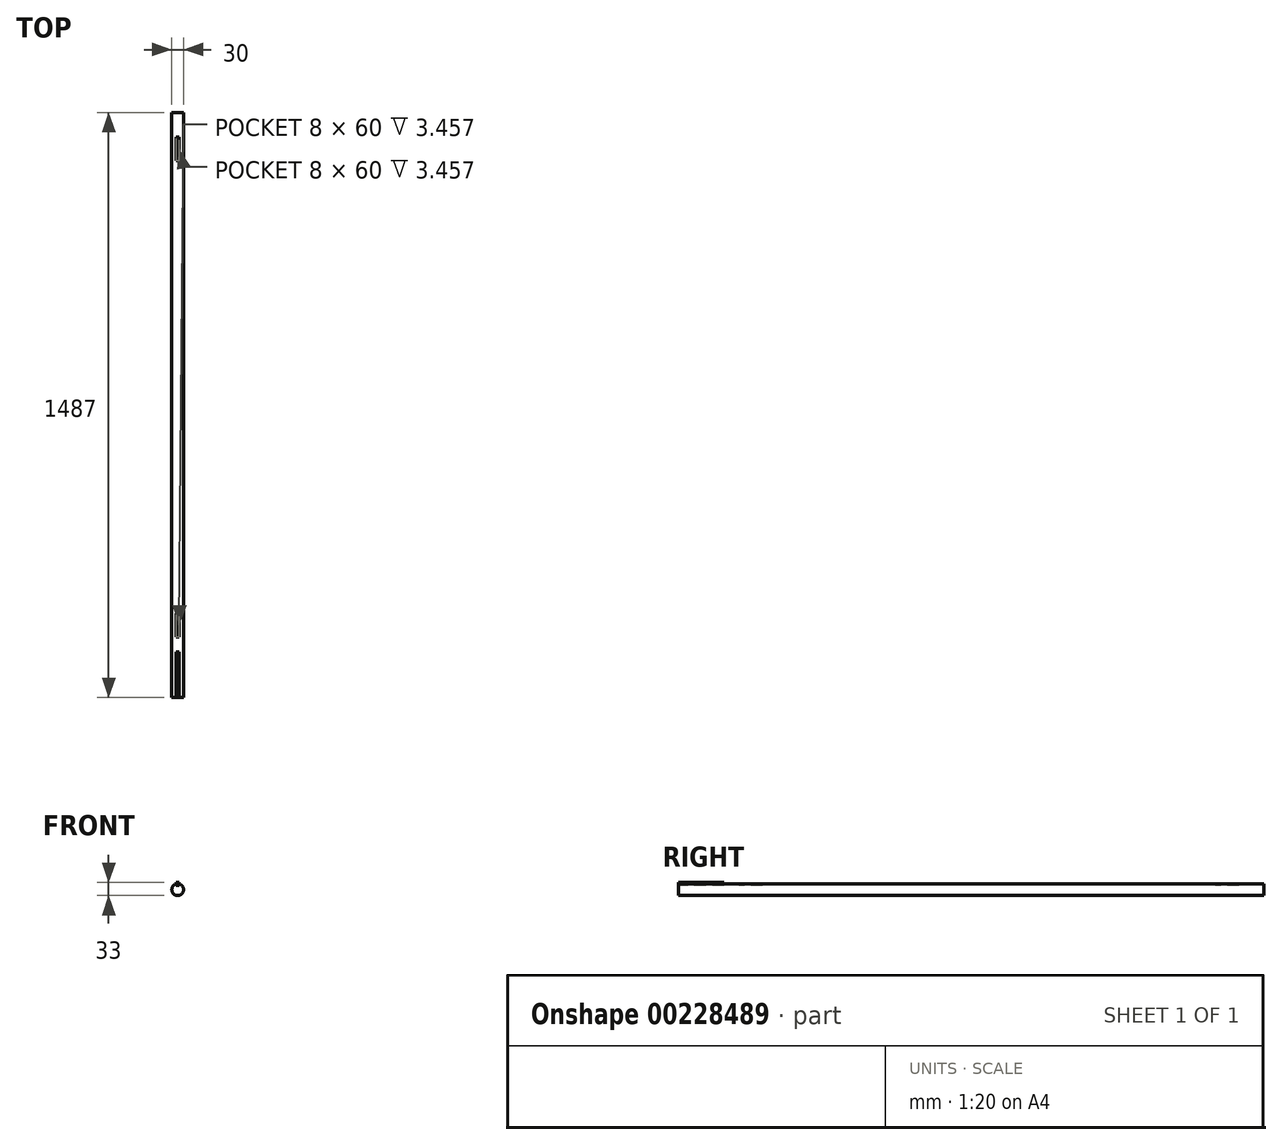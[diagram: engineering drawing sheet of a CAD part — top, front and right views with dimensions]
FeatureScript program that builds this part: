
annotation { "Feature Type Name" : "Feature", "Feature Type Description" : "" }
export const myFeature = defineFeature(function(context is Context, id is Id, definition is map)
    precondition{}
    {
        {
            var Q0;
            Q0=qCreatedBy(makeId("Front.planeOp"),FACE);
            var sketch = newSketch(context, id + "F0", { "sketchPlane" : qUnion([Q0])});
            skCircle(sketch, "E0", {"center": v(0, 0) * mm, "radius": 15 * mm});
            skSolve(sketch);
        }
        {
            var Q0;
            Q0=qSketchRegion(id+"F0",true);
            extrude(context, id + "F1", {"entities" : qUnion([Q0]), "depth" : 1487 * mm, "offsetDistance" : 25 * mm, "symmetric" : true});
        }
        {
            var Q0;
            Q0=qCreatedBy(makeId("Top.planeOp"),FACE);
            cPlane(context, id + "F2", {"entities" : qUnion([Q0]), "cplaneType" : CPlaneType.OFFSET, "offset" : 15 * mm, "width" : 150 * mm, "height" : 150 * mm});
        }
        {
            var Q0;
            Q0=qCreatedBy(id+"F2.planeOp",FACE);
            var sketch = newSketch(context, id + "F3", { "sketchPlane" : qUnion([Q0])});
            skLineSegment(sketch, "E1.bottom", {"start": v(-4, 680.5) * mm, "end": v(4, 680.5) * mm});
            skLineSegment(sketch, "E1.top", {"start": v(-4, 620.5) * mm, "end": v(4, 620.5) * mm});
            skLineSegment(sketch, "E1.left", {"start": v(-4, 680.5) * mm, "end": v(-4, 620.5) * mm});
            skLineSegment(sketch, "E1.right", {"start": v(4, 680.5) * mm, "end": v(4, 620.5) * mm});
            skLineSegment(sketch, "E2.bottom", {"start": v(-4, -529.5) * mm, "end": v(4, -529.5) * mm});
            skLineSegment(sketch, "E2.top", {"start": v(-4, -589.5) * mm, "end": v(4, -589.5) * mm});
            skLineSegment(sketch, "E2.left", {"start": v(-4, -529.5) * mm, "end": v(-4, -589.5) * mm});
            skLineSegment(sketch, "E2.right", {"start": v(4, -529.5) * mm, "end": v(4, -589.5) * mm});
            skLineSegment(sketch, "E3.bottom", {"start": v(-4, -627.5) * mm, "end": v(4, -627.5) * mm});
            skLineSegment(sketch, "E3.top", {"start": v(-4, -743.5) * mm, "end": v(4, -743.5) * mm});
            skLineSegment(sketch, "E3.left", {"start": v(-4, -627.5) * mm, "end": v(-4, -743.5) * mm});
            skLineSegment(sketch, "E3.right", {"start": v(4, -627.5) * mm, "end": v(4, -743.5) * mm});
            skSolve(sketch);
        }
        {
            var Q0;
            Q0=qSketchRegion(id+"F3",true);
            extrude(context, id + "F4", {"entities" : qUnion([Q0]), "operationType" : NewBodyOperationType.REMOVE, "oppositeDirection" : true, "depth" : 4 * mm, "offsetDistance" : 25 * mm});
        }
        {
            var Q0;
            Q0=makeQuery(id+"F4.boolean.opBoolean","COPY",FACE,{"derivedFrom":makeQuery(id+"F4.opExtrude","CAP_FACE",FACE,{"disambiguationData":[OSD([sQuery(id+"F3.wireOp",EDGE,"E3.bottom"),sQuery(id+"F3.wireOp",EDGE,"E3.top"),sQuery(id+"F3.wireOp",EDGE,"E3.left"),sQuery(id+"F3.wireOp",EDGE,"E3.right")])],"isStart":false})});
            extrude(context, id + "F5", {"entities" : qUnion([Q0]), "depth" : 7 * mm, "offsetDistance" : 25 * mm});
        }
    });
